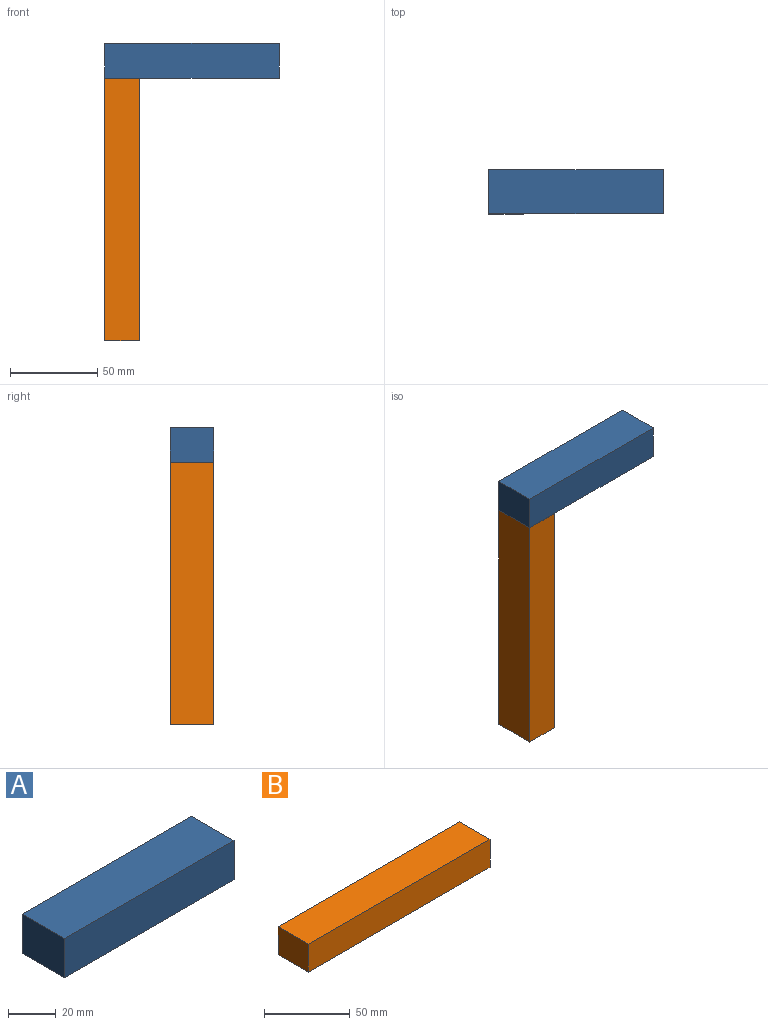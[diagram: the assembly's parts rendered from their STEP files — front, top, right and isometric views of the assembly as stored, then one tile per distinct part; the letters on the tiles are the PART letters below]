
ASSEMBLY  parts=2 mates=1
PART A: 6 faces, bbox 100x25x20 mm
  f0: plane 100x25mm, normal (0,0,-1), area 2500mm2, adj f1,f3,f4,f5
  f1: plane 25x20mm, normal (1,0,0), area 500mm2, adj f0,f2,f4,f5
  f2: plane 100x25mm, normal (0,0,1), area 2500mm2, adj f1,f3,f4,f5
  f3: plane 25x20mm, normal (-1,0,0), area 500mm2, adj f0,f2,f4,f5
  f4: plane 100x20mm, normal (0,-1,0), area 2000mm2, adj f0,f1,f2,f3
  f5: plane 100x20mm, normal (0,1,0), area 2000mm2, adj f0,f1,f2,f3
PART B: 6 faces, bbox 150x25x20 mm
  f0: plane 150x25mm, normal (0,0,-1), area 3750mm2, adj f1,f3,f4,f5
  f1: plane 25x20mm, normal (1,0,0), area 500mm2, adj f0,f2,f4,f5
  f2: plane 150x25mm, normal (0,0,1), area 3750mm2, adj f1,f3,f4,f5
  f3: plane 25x20mm, normal (-1,0,0), area 500mm2, adj f0,f2,f4,f5
  f4: plane 150x20mm, normal (0,-1,0), area 3000mm2, adj f0,f1,f2,f3
  f5: plane 150x20mm, normal (0,1,0), area 3000mm2, adj f0,f1,f2,f3
PLACE A t=(45.98,-33.14,-72.84)mm
PLACE B rot(axis=(0,-1,0),90deg) t=(-34.02,-33.14,-74.98)mm
MATE slider B.f2 <-> A.f3  axis (-1,0,0) through (-54.02,-58.14,-74.98)mm
